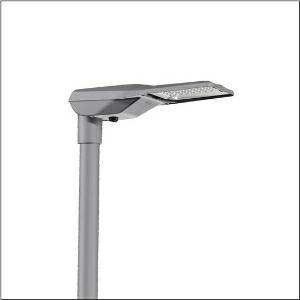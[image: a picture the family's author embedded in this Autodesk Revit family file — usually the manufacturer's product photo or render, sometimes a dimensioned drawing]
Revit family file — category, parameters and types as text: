
# Revit family: streetlight_sl_21_iq_mini___p0_8a_5xe2u31u08jb_01d9
name_source: partatom
category: Lighting Fixtures
units: mm (PartAtom-declared; Revit-internal decimal feet)

## family parameters
Cut with Voids When Loaded = No
Host = Face
Light Source = No
Part Type = Normal
Room Calculation Point = No
Round Connector Dimension = Use Diameter
Shared = No

## types (1)
- --- (1 x LED, 11310 lm, 72.5 W, 3000K)
    Apparent Load = 73 VA
    CIE Flux Codes = 36 69 97 100 100
    Color Rendering = 70
    Color Temperature = 3000K
    Default Elevation = 1800 mm
    Description = Streetlight SL 21 iQ mini, mast luminaire, primary light control with lens, of PMMA, primary optical cover: cover, of toughened safety glass, transparent, light distribution: P0.8a, light emission: direct distribution, primary light characteristic: asymmetric, installation type: post-top, side-entry, LED, High Power LED, rated luminous flux: 11.310lm, luminous efficacy: 156lm/W, light colour: 730, colour temperature: 3000K, control gear: iQ-Street Remote, D4i with power reduction, control: pre-setting: logarithmic dimming characteristic, Street-Remote, Auto-Match, Temp-Guard, Lumen-Switch, Night-Set, Smart-Wire, Light-Fading, Desk-Remote (wireless, voltage-free reading and setting of iQ features in the workshop via application-optimized NFC function/RFID function), optimised constant luminous flux control (CLO 2.0), mains connection: 220..240V, AC, 50/60Hz, start of lifetime: 73W, end of service life: 76W, reduction: 33W, luminaire housing, of diecast aluminium, powder-coated, SITECO metallic grey (DB 702S), corrosivity category C5 high according to DIN EN ISO 12944, please order mast flange separately, inclination adjustable: 0°, 5°, 10°, 15°, sealing non-destructively replaceable, multi-level sealing system, length: 628mm, width: 235mm, height: 110mm, mast flange for spigot size: 42mm (side-entry): 5XC10008XM4, 60/48mm (side-entry/post-top): 5XC10108XM2, 76/60mm (side-entry/post-top): 5XC10108XM1, mounting height: 4..8m, Smart Interface below, protection rating (complete): IP66, insulation class (complete): insulation class II (safety insulation), certification: CE, ENEC, ENEC+, VDE, impact resistance: IK10, permissible operating ambient temperature for outdoor applications: -40..+50°C, standard-compliant lighting for roads and squares, packaging unit: 1 piece

Light Distribution: P0.8a
    Height = 110 mm
    Lamp = 1 x LED
    Lamp Light Flux = 11310 lm
    Lamp Power = 72.5 W
    Lamp count = 1
    Length = 625 mm
    Luminous efficacy = 156 lm/W
    Manufacturer = Siteco
    ModVariant = No
    Model = 5XE2U31U08JB
    Number of Poles = 1
    OnlyDefault = Yes
    Power Factor = 1
    Product Name = Streetlight SL 21 iQ mini | P0.8a
    Product group = mast luminaire | pylon top
    ProductGroupID = 6100
    Protection Class = Protection class II
    Protection Degree = IP 66
    RLX_Detail_Level = 1
    RLX_Emergency_Light_Flux = 0 lm
    RLX_Emergency_Type = 0
    RLX_Emergency_Type_DB = No
    RlxData = <blob elided: 92213 chars, md5=019519c7>
    Socket = socket
    Standby Power = 0 W
    System Light Flux = 11310 lm
    System Power = 73 W
    Type Comments = factory setting: luminous flux: 100 % | dim-lin: 254 | 755 mA
    Type Image = l_1003516.jpg
    URL = http://relux.com
    VarID = @adj_079915
    Voltage = 0 V
    Weight = 0.00 kg
    Width = 234 mm

## geometry (parser evidence)
native form markers: Blend x4, Sweep x11
no freeform markers — native parametric forms only
